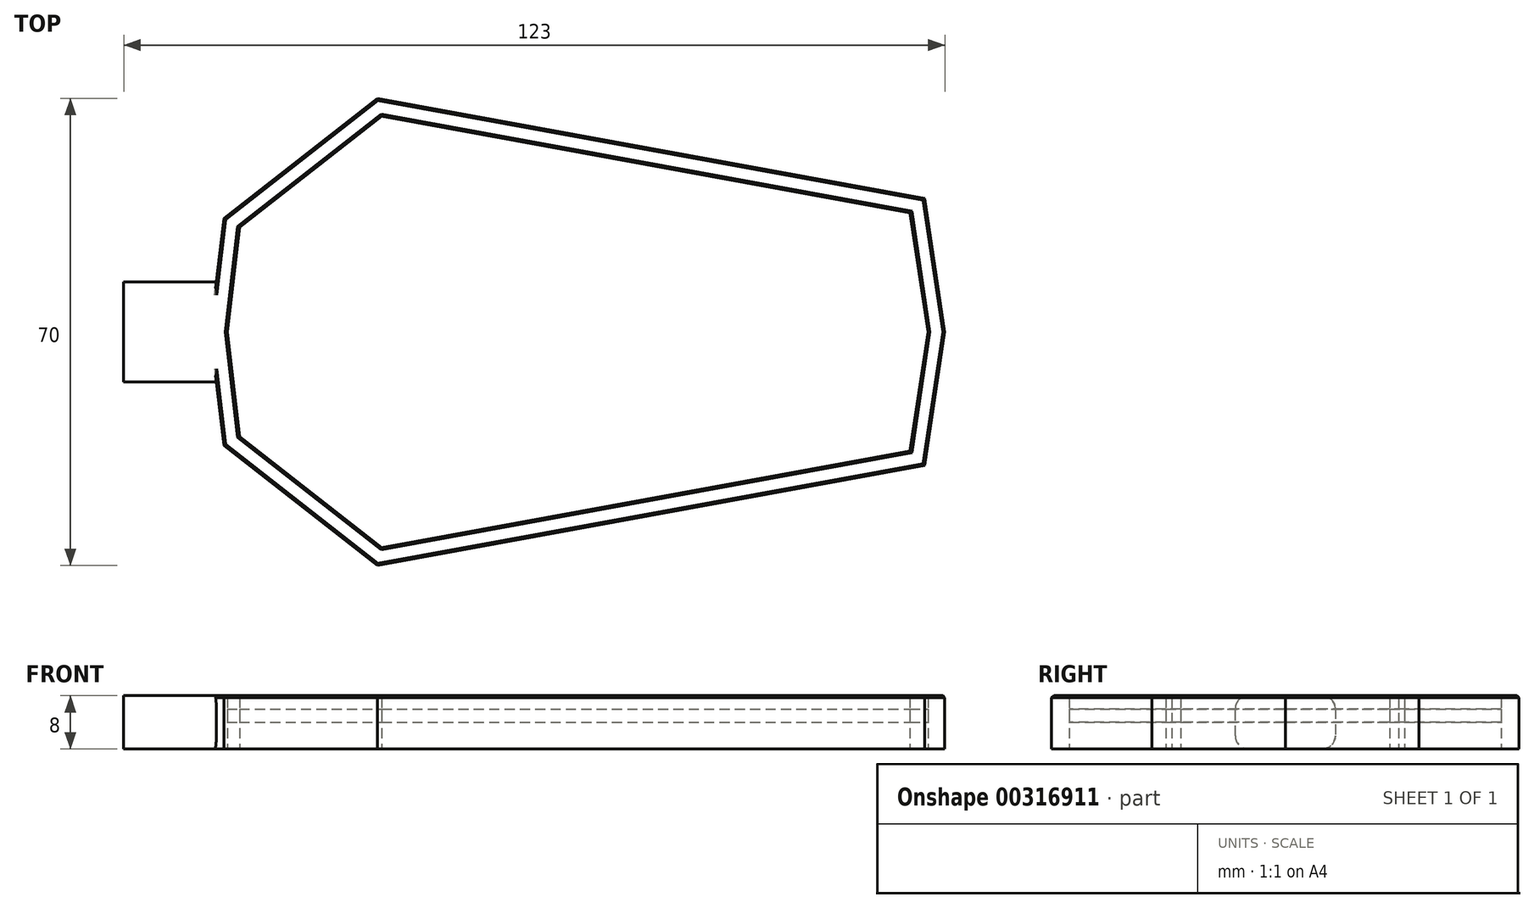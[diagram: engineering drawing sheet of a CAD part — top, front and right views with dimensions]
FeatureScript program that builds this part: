
annotation { "Feature Type Name" : "Feature", "Feature Type Description" : "" }
export const myFeature = defineFeature(function(context is Context, id is Id, definition is map)
    precondition{}
    {
        {
            var Q0;
            Q0=qCreatedBy(makeId("Top.planeOp"),FACE);
            var sketch = newSketch(context, id + "F0", { "sketchPlane" : qUnion([Q0])});
            skLineSegment(sketch, "E0", {"start": v(-46.86, 0) * mm, "end": v(-44.86, 17) * mm});
            skLineSegment(sketch, "E1", {"start": v(-44.86, 17) * mm, "end": v(-21.86, 35) * mm});
            skLineSegment(sketch, "E2", {"start": v(-21.86, 35) * mm, "end": v(60.14, 20) * mm});
            skLineSegment(sketch, "E3", {"start": v(60.14, 20) * mm, "end": v(63.14, 0) * mm});
            skLineSegment(sketch, "E4.MirrorCS", {"start": v(-21.86, -35) * mm, "end": v(60.14, -20) * mm});
            skLineSegment(sketch, "E5.MirrorCS", {"start": v(60.14, -20) * mm, "end": v(63.14, 0) * mm});
            skLineSegment(sketch, "E6.MirrorCS", {"start": v(-46.86, 0) * mm, "end": v(-44.86, -17) * mm});
            skLineSegment(sketch, "E7.MirrorCS", {"start": v(-44.86, -17) * mm, "end": v(-21.86, -35) * mm});
            skLineSegment(sketch, "E8.0", {"start": v(-44.35, 0) * mm, "end": v(-42.5, -15.67) * mm});
            skLineSegment(sketch, "E8.1", {"start": v(-44.35, 0) * mm, "end": v(-42.5, 15.67) * mm});
            skLineSegment(sketch, "E8.2", {"start": v(-42.5, -15.67) * mm, "end": v(-21.2, -32.34) * mm});
            skLineSegment(sketch, "E8.3", {"start": v(-42.5, 15.67) * mm, "end": v(-21.2, 32.34) * mm});
            skLineSegment(sketch, "E8.4", {"start": v(-21.2, -32.34) * mm, "end": v(57.93, -17.86) * mm});
            skLineSegment(sketch, "E8.5", {"start": v(57.93, -17.86) * mm, "end": v(60.6, 0) * mm});
            skLineSegment(sketch, "E8.6", {"start": v(57.93, 17.86) * mm, "end": v(60.6, 0) * mm});
            skLineSegment(sketch, "E8.7", {"start": v(-21.2, 32.34) * mm, "end": v(57.93, 17.86) * mm});
            skSolve(sketch);
        }
        {
            var Q0;
            Q0 = qSketchRegion(id + "F0", true);
            extrude(context, id + "F1", {"entities" : qUnion([Q0]), "endBound" : BoundingType.SYMMETRIC, "depth" : 8 * mm});
        }
        {
            var Q0;
            Q0=makeQuery(id+"F0.imprint","IMPRINT",FACE,{"disambiguationData":[TD([[makeQuery(id+"F0.imprint","IMPRINT",EDGE,{"derivedFrom":sQuery(id+"F0.wireOp",EDGE,"E8.0")}),1.0]])]});
            extrude(context, id + "F2", {"entities" : qUnion([Q0]), "depth" : 2 * mm});
        }
        {
            var Q0;
            Q0=makeQuery(id+"F1.opExtrude","SWEPT_EDGE",EDGE,{"disambiguationData":[OSD([sQuery(id+"F0.wireOp",EDGE,"E0"),sQuery(id+"F0.wireOp",EDGE,"E1")])]});
            cPoint(context, id + "F3", {"entities" : qUnion([Q0]), "parameter" : 0.5});
        }
        {
            var Q0;
            Q0=qCreatedBy(makeId("Right.planeOp"),FACE);
            var Q1;
            Q1 = qCreatedBy(id + "F3" ,VERTEX);
            cPlane(context, id + "F4", {"entities" : qUnion([Q0, Q1]), "cplaneType" : CPlaneType.PLANE_POINT, "offset" : 25 * mm, "width" : 150 * mm, "height" : 150 * mm});
        }
        {
            var Q0;
            Q0=qCreatedBy(id+"F4.planeOp",FACE);
            var sketch = newSketch(context, id + "F5", { "sketchPlane" : qUnion([Q0])});
            skLineSegment(sketch, "E9.bottom", {"start": v(-7.5, -4) * mm, "end": v(7.5, -4) * mm});
            skLineSegment(sketch, "E9.top", {"start": v(-7.5, 4) * mm, "end": v(7.5, 4) * mm});
            skLineSegment(sketch, "E9.left", {"start": v(-7.5, -4) * mm, "end": v(-7.5, 4) * mm});
            skLineSegment(sketch, "E9.right", {"start": v(7.5, -4) * mm, "end": v(7.5, 4) * mm});
            skPoint(sketch, "E9.middle", {"position": v(0, 0) * mm});
            skSolve(sketch);
        }
        {
            var Q0;
            Q0 = qSketchRegion(id + "F5", true);
            extrude(context, id + "F6", {"entities" : qUnion([Q0]), "operationType" : NewBodyOperationType.ADD, "oppositeDirection" : true, "depth" : 15 * mm});
        }
        {
            var Q0;
            Q0=makeQuery(id+"F6.opExtrude","SWEPT_EDGE",EDGE,{"disambiguationData":[OSD([sQuery(id+"F5.wireOp",EDGE,"E9.bottom"),sQuery(id+"F5.wireOp",EDGE,"E9.left")])]});
            var Q1;
            Q1=makeQuery(id+"F6.opExtrude","SWEPT_EDGE",EDGE,{"disambiguationData":[OSD([sQuery(id+"F5.wireOp",EDGE,"E9.top"),sQuery(id+"F5.wireOp",EDGE,"E9.left")])]});
            var Q2;
            Q2=makeQuery(id+"F6.opExtrude","SWEPT_EDGE",EDGE,{"disambiguationData":[OSD([sQuery(id+"F5.wireOp",EDGE,"E9.bottom"),sQuery(id+"F5.wireOp",EDGE,"E9.right")])]});
            var Q3;
            Q3=makeQuery(id+"F6.opExtrude","SWEPT_EDGE",EDGE,{"disambiguationData":[OSD([sQuery(id+"F5.wireOp",EDGE,"E9.top"),sQuery(id+"F5.wireOp",EDGE,"E9.right")])]});
            fillet(context, id + "F7", {"entities" : qUnion([Q0, Q1, Q2, Q3]), "radius" : 2 * mm, "tangentPropagation" : true, "allowEdgeOverflow" : false});
        }
        {
            var Q0;
            Q0=makeQuery(id+"F1.opExtrude","CAP_EDGE",EDGE,{"disambiguationData":[OSD([sQuery(id+"F0.wireOp",EDGE,"E7.MirrorCS")])],"isStart":false});
            var Q1;
            Q1=makeQuery(id+"F1.opExtrude","CAP_EDGE",EDGE,{"disambiguationData":[OSD([sQuery(id+"F0.wireOp",EDGE,"E4.MirrorCS")])],"isStart":false});
            var Q2;
            Q2=makeQuery(id+"F1.opExtrude","CAP_EDGE",EDGE,{"disambiguationData":[OSD([sQuery(id+"F0.wireOp",EDGE,"E6.MirrorCS")])],"isStart":false});
            var Q3;
            Q3=makeQuery(id+"F1.opExtrude","CAP_EDGE",EDGE,{"disambiguationData":[OSD([sQuery(id+"F0.wireOp",EDGE,"E0")])],"isStart":false});
            var Q4;
            Q4=makeQuery(id+"F1.opExtrude","CAP_EDGE",EDGE,{"disambiguationData":[OSD([sQuery(id+"F0.wireOp",EDGE,"E1")])],"isStart":false});
            var Q5;
            Q5=makeQuery(id+"F1.opExtrude","CAP_EDGE",EDGE,{"disambiguationData":[OSD([sQuery(id+"F0.wireOp",EDGE,"E2")])],"isStart":false});
            var Q6;
            Q6=makeQuery(id+"F1.opExtrude","CAP_EDGE",EDGE,{"disambiguationData":[OSD([sQuery(id+"F0.wireOp",EDGE,"E3")])],"isStart":false});
            var Q7;
            Q7=makeQuery(id+"F1.opExtrude","CAP_EDGE",EDGE,{"disambiguationData":[OSD([sQuery(id+"F0.wireOp",EDGE,"E5.MirrorCS")])],"isStart":false});
            var Q8;
            Q8=makeQuery(id+"F1.opExtrude","CAP_EDGE",EDGE,{"disambiguationData":[OSD([sQuery(id+"F0.wireOp",EDGE,"E8.2")])],"isStart":false});
            var Q9;
            Q9=makeQuery(id+"F1.opExtrude","CAP_EDGE",EDGE,{"disambiguationData":[OSD([sQuery(id+"F0.wireOp",EDGE,"E8.0")])],"isStart":false});
            var Q10;
            Q10=makeQuery(id+"F1.opExtrude","CAP_EDGE",EDGE,{"disambiguationData":[OSD([sQuery(id+"F0.wireOp",EDGE,"E8.1")])],"isStart":false});
            var Q11;
            Q11=makeQuery(id+"F1.opExtrude","CAP_EDGE",EDGE,{"disambiguationData":[OSD([sQuery(id+"F0.wireOp",EDGE,"E8.3")])],"isStart":false});
            var Q12;
            Q12=makeQuery(id+"F1.opExtrude","CAP_EDGE",EDGE,{"disambiguationData":[OSD([sQuery(id+"F0.wireOp",EDGE,"E8.7")])],"isStart":false});
            var Q13;
            Q13=makeQuery(id+"F1.opExtrude","CAP_EDGE",EDGE,{"disambiguationData":[OSD([sQuery(id+"F0.wireOp",EDGE,"E8.4")])],"isStart":false});
            var Q14;
            Q14=makeQuery(id+"F1.opExtrude","CAP_EDGE",EDGE,{"disambiguationData":[OSD([sQuery(id+"F0.wireOp",EDGE,"E8.5")])],"isStart":false});
            var Q15;
            Q15=makeQuery(id+"F1.opExtrude","CAP_EDGE",EDGE,{"disambiguationData":[OSD([sQuery(id+"F0.wireOp",EDGE,"E8.6")])],"isStart":false});
            chamfer(context, id + "F8", {"entities" : qUnion([Q0, Q1, Q2, Q3, Q4, Q5, Q6, Q7, Q8, Q9, Q10, Q11, Q12, Q13, Q14, Q15]), "width" : .3 * mm, "tangentPropagation" : true});
        }
    });
